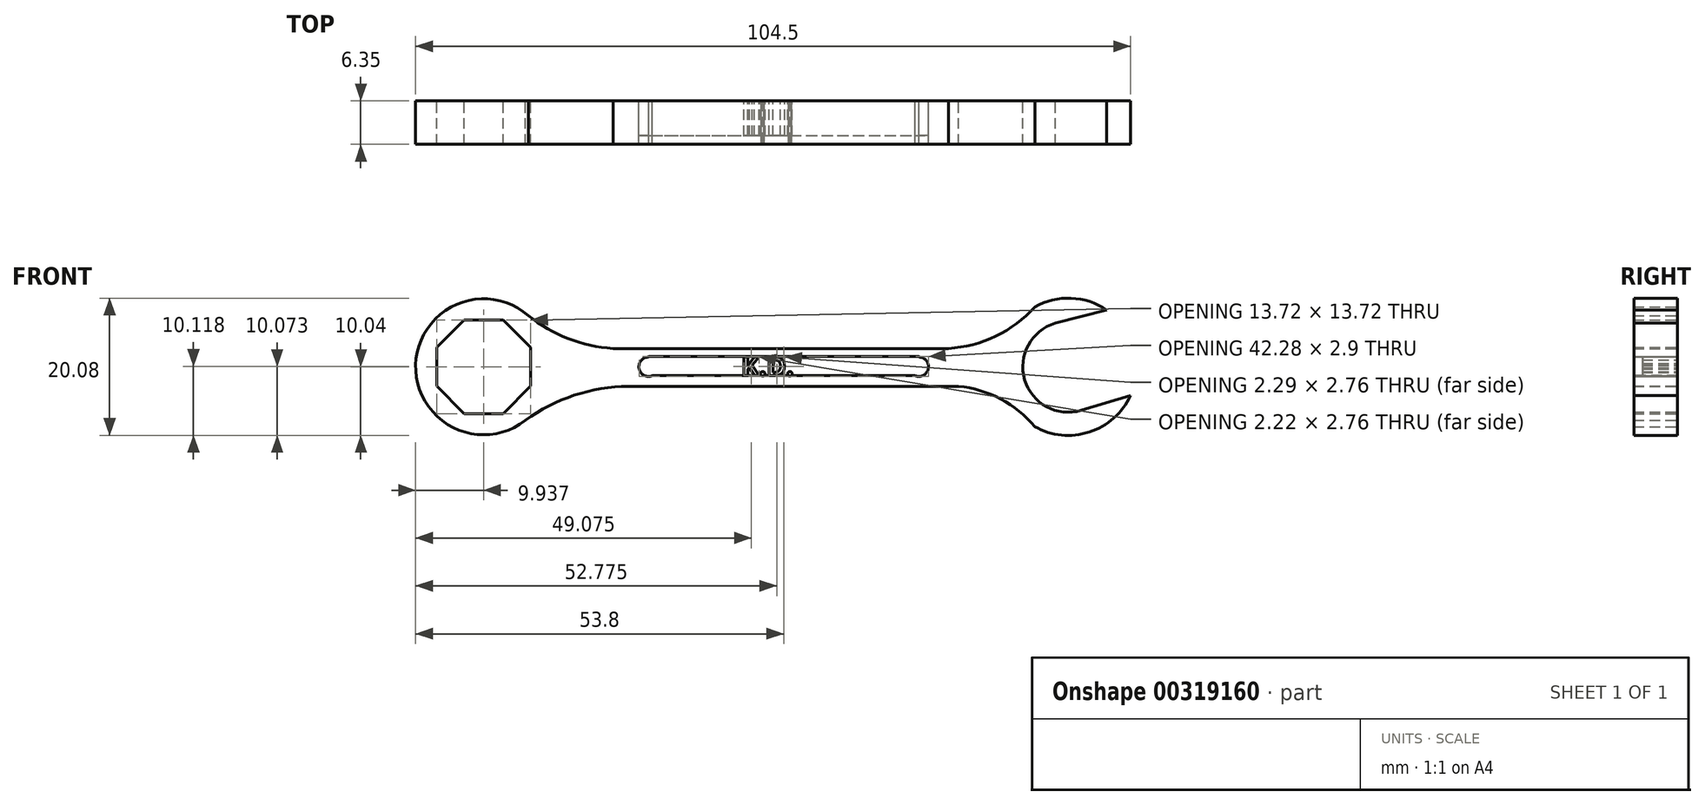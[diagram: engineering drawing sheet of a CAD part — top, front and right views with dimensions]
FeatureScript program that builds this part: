
annotation { "Feature Type Name" : "Feature", "Feature Type Description" : "" }
export const myFeature = defineFeature(function(context is Context, id is Id, definition is map)
    precondition{}
    {
        {
            var Q0;
            Q0=qCreatedBy(makeId("Front.planeOp"),FACE);
            var sketch = newSketch(context, id + "F0", { "sketchPlane" : qUnion([Q0])});
            skCircle(sketch, "E0", {"center": v(-76.31, 0) * mm, "radius": 9.94 * mm});
            skCircle(sketch, "E1.cCircle", {"center": v(-76.31, 0) * mm, "radius": 6.86 * mm, "construction": true});
            skLineSegment(sketch, "E1.0", {"start": v(-69.45, 2.84) * mm, "end": v(-69.45, -2.84) * mm});
            skLineSegment(sketch, "E1.1", {"start": v(-69.45, -2.84) * mm, "end": v(-73.47, -6.86) * mm});
            skLineSegment(sketch, "E1.2", {"start": v(-73.47, -6.86) * mm, "end": v(-79.16, -6.86) * mm});
            skLineSegment(sketch, "E1.3", {"start": v(-79.16, -6.86) * mm, "end": v(-83.17, -2.84) * mm});
            skLineSegment(sketch, "E1.4", {"start": v(-83.17, -2.84) * mm, "end": v(-83.17, 2.84) * mm});
            skLineSegment(sketch, "E1.5", {"start": v(-83.17, 2.84) * mm, "end": v(-79.16, 6.86) * mm});
            skLineSegment(sketch, "E1.6", {"start": v(-79.16, 6.86) * mm, "end": v(-73.47, 6.86) * mm});
            skLineSegment(sketch, "E1.7", {"start": v(-73.47, 6.86) * mm, "end": v(-69.45, 2.84) * mm});
            skPoint(sketch, "E1.0.midPoint", {"position": v(-69.45, 0) * mm});
            skLineSegment(sketch, "E2.bottom", {"start": v(-57.41, 2.68) * mm, "end": v(-8.35, 2.68) * mm});
            skLineSegment(sketch, "E2.top", {"start": v(-55.13, -2.85) * mm, "end": v(-6.9, -2.85) * mm});
            skArc(sketch, "E3", {"start": v(-70.22, 7.85) * mm, "mid": v(-62.92, 3.75) * mm, "end": v(-54.62, 2.68) * mm});
            skArc(sketch, "E4", {"start": v(-54.62, -2.85) * mm, "mid": v(-62.82, -4.1) * mm, "end": v(-70.22, -7.85) * mm});
            skArc(sketch, "E5", {"start": v(14.75, 8.33) * mm, "mid": v(9.56, 10.03) * mm, "end": v(4.24, 8.76) * mm});
            skArc(sketch, "E6", {"start": v(-10.42, 2.68) * mm, "mid": v(-2.4, 4.04) * mm, "end": v(4.24, 8.76) * mm});
            skArc(sketch, "E7", {"start": v(4.24, -8.76) * mm, "mid": v(-2.35, -3.98) * mm, "end": v(-10.42, -2.85) * mm});
            skArc(sketch, "E8", {"start": v(7.69, 6.49) * mm, "mid": v(2.71, -1.68) * mm, "end": v(11.04, -6.37) * mm});
            skLineSegment(sketch, "E9", {"start": v(7.25, 6.37) * mm, "end": v(14.75, 8.33) * mm});
            skLineSegment(sketch, "E10", {"start": v(11.04, -6.37) * mm, "end": v(18.25, -4.23) * mm});
            skLineSegment(sketch, "E11.trimOffspring", {"start": v(-0.53, 2.68) * mm, "end": v(0.02, 2.68) * mm});
            skLineSegment(sketch, "E12.trimOffspring", {"start": v(-0.48, -2.85) * mm, "end": v(0, -2.85) * mm});
            skArc(sketch, "E13.trimOffspring", {"start": v(4.24, -8.76) * mm, "mid": v(12.23, -9.55) * mm, "end": v(18.25, -4.23) * mm});
            skArc(sketch, "E14.trimOffspring", {"start": v(1.03, 5.91) * mm, "mid": v(-0.9, 0.12) * mm, "end": v(0.9, -5.72) * mm});
            skLineSegment(sketch, "E15.bottom", {"start": v(-52.2, -1.3) * mm, "end": v(-12.7, -1.3) * mm});
            skLineSegment(sketch, "E15.top", {"start": v(-52.2, 1.48) * mm, "end": v(-12.7, 1.48) * mm});
            skArc(sketch, "E16", {"start": v(-52.2, 1.42) * mm, "mid": v(-53.59, -0.29) * mm, "end": v(-51.64, -1.3) * mm});
            skArc(sketch, "E17", {"start": v(-13.26, -1.3) * mm, "mid": v(-11.31, -0.29) * mm, "end": v(-12.7, 1.42) * mm});
            skLineSegment(sketch, "E18.trimOffspring", {"start": v(-52.2, 1.42) * mm, "end": v(-52.2, 1.48) * mm});
            skLineSegment(sketch, "E19.trimOffspring", {"start": v(-12.7, 1.42) * mm, "end": v(-12.7, 1.48) * mm});
            skText(sketch, "E20", { "text": "K.D.", "fontName": "OpenSans-Bold.ttf"});
            const initialGuessF0  = {"E20": [-0.03863, -0.0013, 1, 0, 0.00278]};
            skSetInitialGuess(sketch, initialGuessF0);
            skSolve(sketch);
        }
        {
            var Q0;
            {var subQ0=sQuery(id+"F0.wireOp",EDGE,"E20.sketch_text.stroke-1");Q0=makeQuery(id+"F0.imprint","IMPRINT",FACE,{"disambiguationData":[TD([[makeQuery(id+"F0.imprint","IMPRINT",EDGE,{"derivedFrom":subQ0}),1.0]])]});}
            var Q1;
            Q1=makeQuery(id+"F0.imprint","IMPRINT",FACE,{"disambiguationData":[TD([[makeQuery(id+"F0.imprint","IMPRINT",EDGE,{"derivedFrom":sQuery(id+"F0.wireOp",EDGE,"E20.sketch_text.stroke-28")}),1.0]])]});
            var Q2;
            Q2=makeQuery(id+"F0.imprint","IMPRINT",FACE,{"disambiguationData":[TD([[makeQuery(id+"F0.imprint","IMPRINT",EDGE,{"derivedFrom":sQuery(id+"F0.wireOp",EDGE,"E15.top")}),-1.0]])]});
            extrude(context, id + "F1", {"entities" : qUnion([Q0, Q1, Q2]), "depth" : 5.08 * mm});
        }
        {
            var Q0;
            Q0 = qSketchRegion(id + "F0", true);
            extrude(context, id + "F2", {"entities" : qUnion([Q0]), "depth" : 6.35 * mm});
        }
    });
